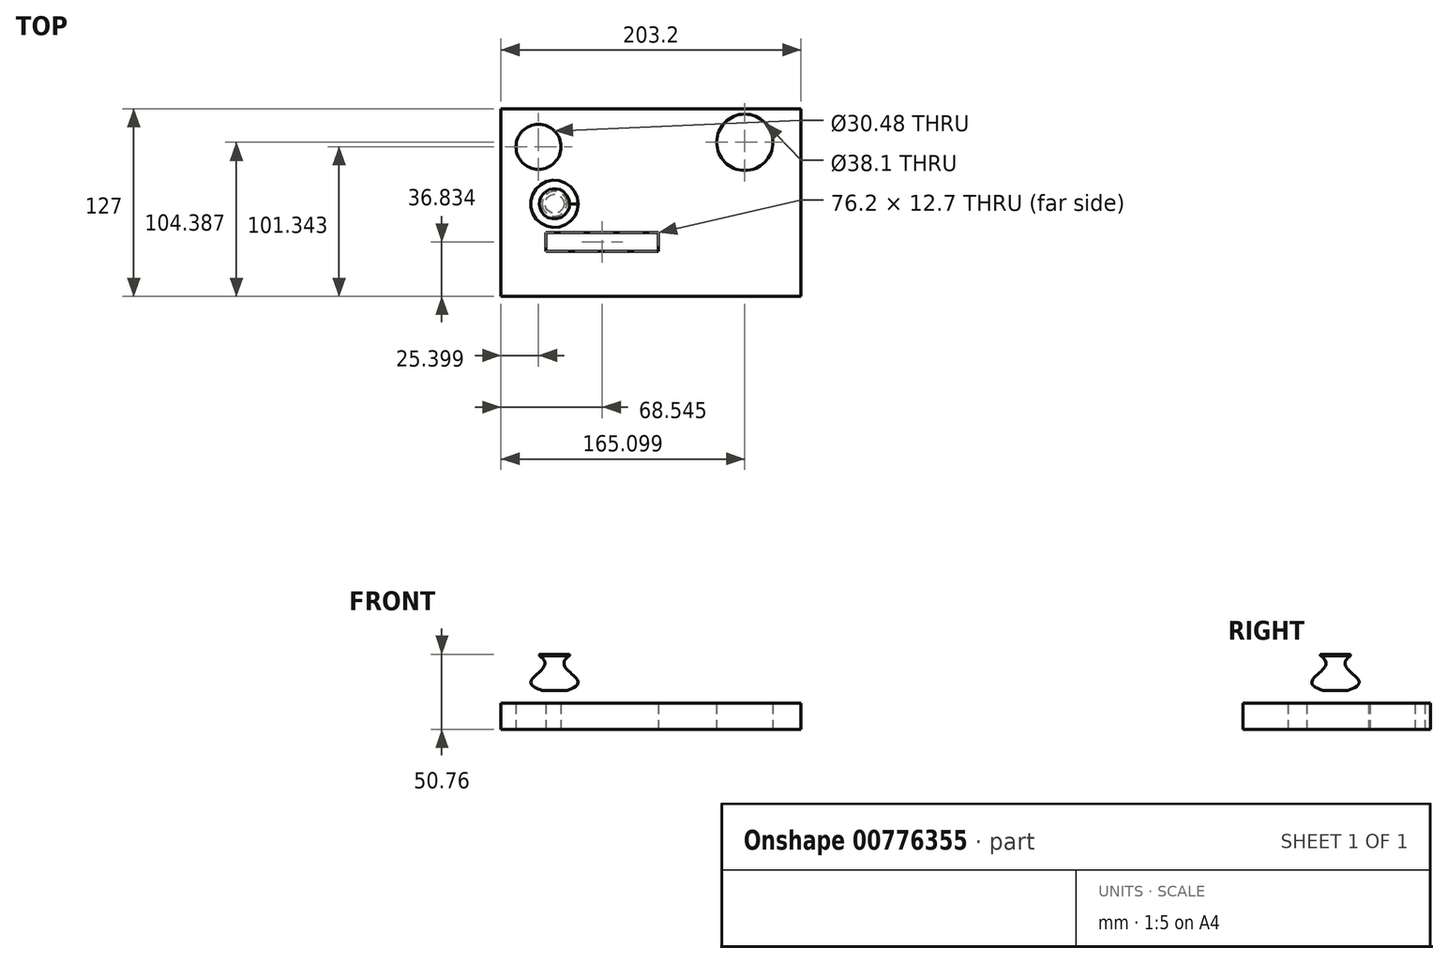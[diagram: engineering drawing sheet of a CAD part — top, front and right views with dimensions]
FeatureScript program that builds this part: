
annotation { "Feature Type Name" : "Feature", "Feature Type Description" : "" }
export const myFeature = defineFeature(function(context is Context, id is Id, definition is map)
    precondition{}
    {
        {
            var Q0;
            Q0=qCreatedBy(makeId("Top.planeOp"),FACE);
            var sketch = newSketch(context, id + "F0", { "sketchPlane" : qUnion([Q0])});
            skLineSegment(sketch, "E0.bottom", {"start": v(-62.93, 64.3) * mm, "end": v(140.27, 64.3) * mm});
            skLineSegment(sketch, "E0.top", {"start": v(-62.93, -62.7) * mm, "end": v(140.27, -62.7) * mm});
            skLineSegment(sketch, "E0.left", {"start": v(-62.93, 64.3) * mm, "end": v(-62.93, -62.7) * mm});
            skLineSegment(sketch, "E0.right", {"start": v(140.27, 64.3) * mm, "end": v(140.27, -62.7) * mm});
            skCircle(sketch, "E1", {"center": v(-37.53, 38.64) * mm, "radius": 15.24 * mm});
            skCircle(sketch, "E2", {"center": v(102.17, 41.69) * mm, "radius": 19.05 * mm});
            skLineSegment(sketch, "E3.bottom", {"start": v(-32.49, -19.52) * mm, "end": v(43.71, -19.52) * mm});
            skLineSegment(sketch, "E3.top", {"start": v(-32.49, -32.22) * mm, "end": v(43.71, -32.22) * mm});
            skLineSegment(sketch, "E3.left", {"start": v(-32.49, -19.52) * mm, "end": v(-32.49, -32.22) * mm});
            skLineSegment(sketch, "E3.right", {"start": v(43.71, -19.52) * mm, "end": v(43.71, -32.22) * mm});
            skSolve(sketch);
        }
        {
            var Q0;
            Q0=makeQuery(id+"F0.imprint","IMPRINT",FACE,{"disambiguationData":[TD([[makeQuery(id+"F0.imprint","IMPRINT",EDGE,{"derivedFrom":sQuery(id+"F0.wireOp",EDGE,"E0.bottom")}),-1.0]])]});
            extrude(context, id + "F1", {"entities" : qUnion([Q0]), "depth" : 17.78 * mm, "offsetDistance" : 25.4 * mm});
        }
        {
            var Q0;
            Q0=qCreatedBy(makeId("Front.planeOp"),FACE);
            var sketch = newSketch(context, id + "F2", { "sketchPlane" : qUnion([Q0])});
            skLineSegment(sketch, "E4", {"start": v(-38.16, 50.76) * mm, "end": v(-26.7, 50.76) * mm});
            skFitSpline(sketch, "E5", {"points": [v(-38.16, 50.76) * mm, v(-35.06, 26.4) * mm], "startDerivative": vector(53.8, -31.7) * mm, "endDerivative": vector(69.1, -21.96) * mm});
            skLineSegment(sketch, "E6", {"start": v(-26.7, 50.76) * mm, "end": v(-26.7, 26.71) * mm});
            skLineSegment(sketch, "E7", {"start": v(-35.06, 26.4) * mm, "end": v(-26.7, 26.71) * mm});
            skSolve(sketch);
        }
        {
            var Q0;
            Q0=makeQuery(id+"F2.imprint","IMPRINT",FACE,{"disambiguationData":[TD([[makeQuery(id+"F2.imprint","IMPRINT",EDGE,{"derivedFrom":sQuery(id+"F2.wireOp",EDGE,"E4")}),-1.0]])]});
            var Q1;
            Q1=sQuery(id+"F2.wireOp",EDGE,"E6");
            revolve(context, id + "F3", {"surfaceOperationType" : NewSurfaceOperationType.NEW, "entities" : qUnion([Q0]), "axis" : qUnion([Q1]), "revolveType" : RevolveType.FULL});
        }
        {
            var Q0;
            Q0=makeQuery(id+"F3.opRevolve","SWEPT_FACE",FACE,{"disambiguationData":[OSD([sQuery(id+"F2.wireOp",EDGE,"E4")])]});
            fillet(context, id + "F4", {"entities" : qUnion([Q0]), "radius" : 0.5 * mm, "tangentPropagation" : true, "allowEdgeOverflow" : false});
        }
    });
